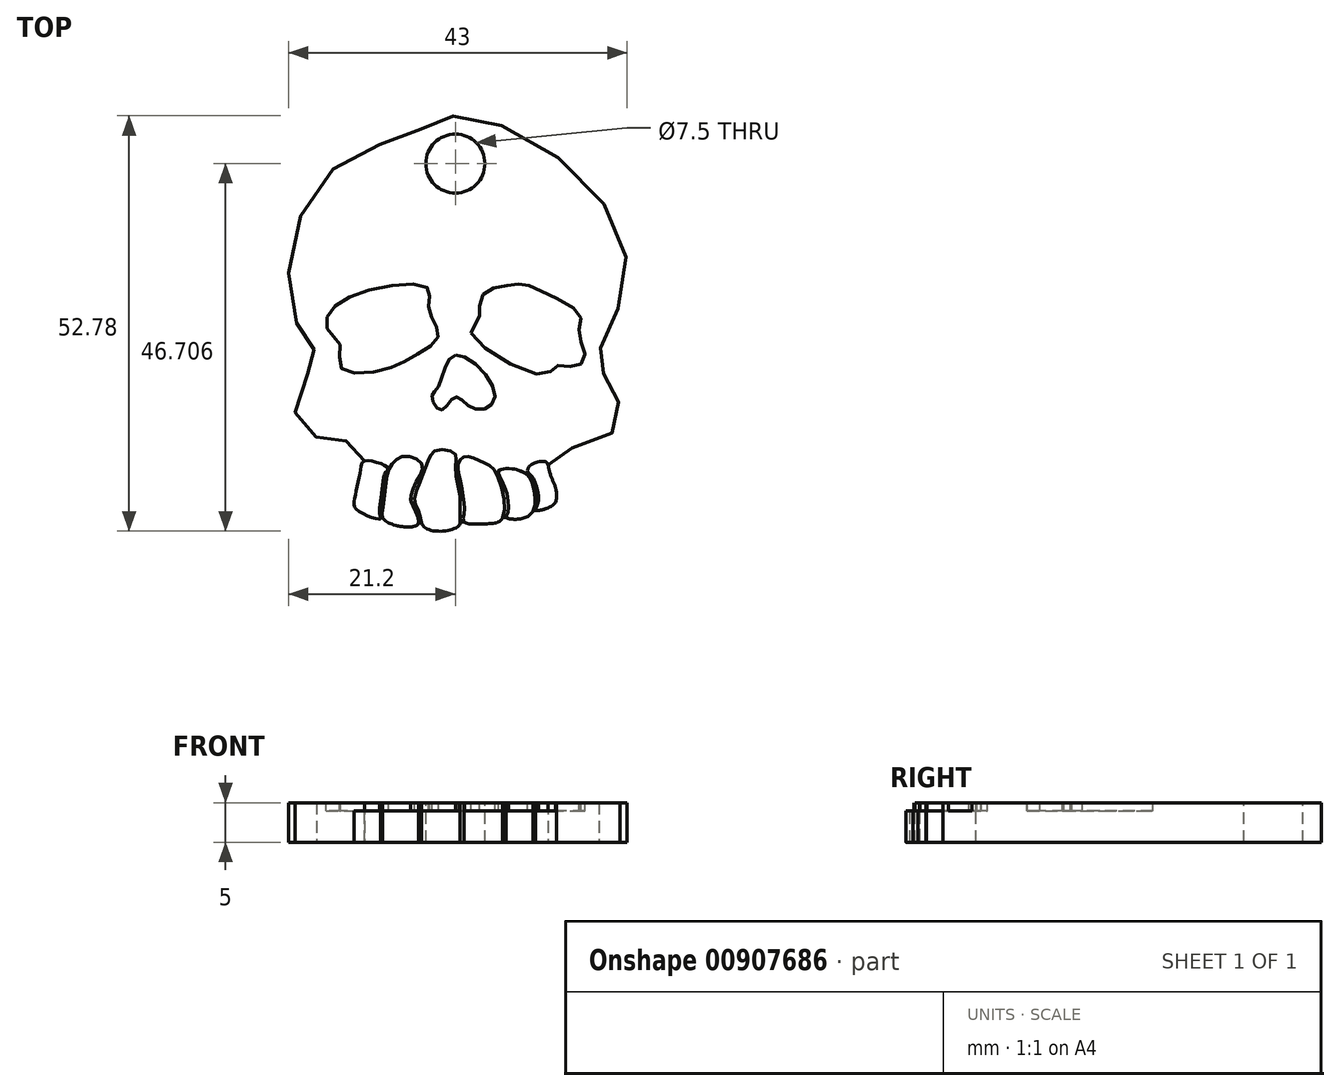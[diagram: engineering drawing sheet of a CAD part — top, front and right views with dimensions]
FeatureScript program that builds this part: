
annotation { "Feature Type Name" : "Feature", "Feature Type Description" : "" }
export const myFeature = defineFeature(function(context is Context, id is Id, definition is map)
    precondition{}
    {
        {
            var Q0;
            Q0=qCreatedBy(makeId("Top.planeOp"),FACE);
            var sketch = newSketch(context, id + "F0", { "sketchPlane" : qUnion([Q0])});
            skPoint(sketch, "E0.middle", {"position": v(0, 0) * mm});
            skFitSpline(sketch, "E1", {"points": [v(-18.77, -2.84) * mm, v(-21.2, 5.84) * mm, v(-15.52, 19.31) * mm, v(-5.25, 23.95) * mm, v(0, 26.05) * mm, v(13.9, 20.07) * mm, v(21.8, 6.43) * mm, v(18.54, -3.21) * mm, v(18.66, -6.34) * mm, v(20.79, -10.47) * mm, v(19.29, -14.73) * mm, v(12.15, -17.23) * mm, v(12.4, -20.36) * mm, v(12.03, -23.24) * mm, v(-11.76, -23.87) * mm, v(-11.5, -17.73) * mm, v(-13.89, -15.23) * mm, v(-18.04, -14.58) * mm, v(-20.36, -10.37) * mm, v(-17.64, -4.46) * mm, v(-18.77, -2.84) * mm]});
            skSolve(sketch);
        }
        {
            var Q0;
            Q0 = qSketchRegion(id + "F0", true);
            extrude(context, id + "F1", {"entities" : qUnion([Q0]), "depth" : 5 * mm, "offsetDistance" : 25 * mm});
        }
        {
            var Q0;
            Q0=makeQuery(id+"F1.opExtrude","CAP_FACE",FACE,{"disambiguationData":[OSD([sQuery(id+"F0.wireOp",EDGE,"E1")])],"isStart":false});
            var sketch = newSketch(context, id + "F2", { "sketchPlane" : qUnion([Q0])});
            skFitSpline(sketch, "E2", {"points": [v(0, -4.32) * mm, v(-2.08, -8.19) * mm, v(-2.98, -9.68) * mm, v(-1.79, -11.31) * mm, v(0, -9.68) * mm, v(2.38, -11.16) * mm, v(5.06, -9.53) * mm, v(0, -4.32) * mm]});
            skFitSpline(sketch, "E3", {"points": [v(2, -1.54) * mm, v(2.9, 0) * mm, v(3.05, 1.3) * mm, v(3.72, 3.6) * mm, v(6.62, 4.5) * mm, v(8.78, 4.64) * mm, v(11.6, 3.45) * mm, v(15.85, 0.7) * mm, v(15.7, -1.61) * mm, v(16.45, -4.29) * mm, v(15.33, -5.78) * mm, v(12.87, -5.7) * mm, v(11.24, -6.82) * mm, v(2, -1.54) * mm]});
            skFitSpline(sketch, "E4", {"points": [v(-2.2, -2.04) * mm, v(-5.03, -4.35) * mm, v(-9.34, -6.29) * mm, v(-14.55, -5.91) * mm, v(-14.63, -3.01) * mm, v(-16.12, -1.37) * mm, v(-15.97, 1.08) * mm, v(-10.31, 4.06) * mm, v(-3.46, 4.13) * mm, v(-3.39, 2.27) * mm, v(-2.8, 0) * mm, v(-2.2, -2.04) * mm]});
            skFitSpline(sketch, "E5", {"points": [v(-3.46, -17.74) * mm, v(-2.44, -16.46) * mm, v(0, -16.9) * mm, v(0, -18.45) * mm, v(0.6, -22.61) * mm, v(0.57, -24.56) * mm, v(0.34, -26.1) * mm, v(-3.77, -26.33) * mm, v(-4.61, -24.3) * mm, v(-5.19, -22.88) * mm, v(-4.26, -19.87) * mm, v(-3.46, -17.74) * mm]});
            skFitSpline(sketch, "E6", {"points": [v(0.46, -17.94) * mm, v(0.46, -19.41) * mm, v(1.03, -22.52) * mm, v(1.09, -24.56) * mm, v(1.12, -25.56) * mm, v(3.67, -25.78) * mm, v(6.01, -25.01) * mm, v(5.03, -19.1) * mm, v(3.3, -17.88) * mm, v(1.4, -17.2) * mm, v(0.46, -17.94) * mm]});
            skFitSpline(sketch, "E7", {"points": [v(5.48, -19.1) * mm, v(6.27, -21.07) * mm, v(6.6, -24.52) * mm, v(6.43, -24.94) * mm, v(7.64, -25.2) * mm, v(9.87, -24.16) * mm, v(9.53, -20.13) * mm, v(8.35, -19.1) * mm, v(6.95, -18.78) * mm, v(5.48, -19.1) * mm]});
            skFitSpline(sketch, "E8", {"points": [v(9.17, -19.1) * mm, v(9.61, -18.26) * mm, v(11.27, -17.84) * mm, v(11.8, -18.32) * mm, v(12.75, -21.3) * mm, v(12.84, -22) * mm, v(12.5, -23.29) * mm, v(10.21, -24.05) * mm, v(10.46, -23.26) * mm, v(9.9, -20.05) * mm, v(9.17, -19.1) * mm]});
            skFitSpline(sketch, "E9", {"points": [v(-4.2, -18.26) * mm, v(-4.9, -20.32) * mm, v(-5.68, -22.58) * mm, v(-5.18, -23.92) * mm, v(-4.68, -25.64) * mm, v(-5.5, -26.16) * mm, v(-7.94, -25.87) * mm, v(-9.22, -25.04) * mm, v(-9.18, -23.53) * mm, v(-8.76, -20.1) * mm, v(-8.05, -18.18) * mm, v(-6.34, -17.16) * mm, v(-4.2, -18.26) * mm]});
            skFitSpline(sketch, "E10", {"points": [v(-8.6, -18.63) * mm, v(-11.5, -17.8) * mm, v(-12.05, -18.87) * mm, v(-12.79, -22.55) * mm, v(-12.47, -24.03) * mm, v(-9.55, -25.16) * mm, v(-9.63, -24.55) * mm, v(-9.42, -22.47) * mm, v(-8.94, -19.42) * mm, v(-8.6, -18.63) * mm]});
            skSolve(sketch);
        }
        {
            var Q0;
            {var subQ0=sQuery(id+"F2.wireOp",EDGE,"E5");var subQ1=makeQuery(id+"F1.opExtrude","CAP_EDGE",EDGE,{"disambiguationData":[OSD([sQuery(id+"F0.wireOp",EDGE,"E1")])],"isStart":false});var subQ2=makeQuery(id+"F2.imprint","INTERSECT",VERTEX,{"disambiguationData":[OD(0.0)],"derivedFrom":[subQ1,subQ0]});Q0=makeQuery(id+"F2.imprint","IMPRINT",FACE,{"disambiguationData":[TD([[makeQuery(id+"F2.imprint","IMPRINT",EDGE,{"disambiguationData":[TD([[subQ2,-1.0]])],"derivedFrom":subQ0}),-1.0]])]});}
            var Q1;
            {var subQ0=sQuery(id+"F2.wireOp",EDGE,"E6");var subQ1=makeQuery(id+"F1.opExtrude","CAP_EDGE",EDGE,{"disambiguationData":[OSD([sQuery(id+"F0.wireOp",EDGE,"E1")])],"isStart":false});var subQ2=makeQuery(id+"F2.imprint","INTERSECT",VERTEX,{"disambiguationData":[OD(0.0)],"derivedFrom":[subQ1,subQ0]});Q1=makeQuery(id+"F2.imprint","IMPRINT",FACE,{"disambiguationData":[TD([[makeQuery(id+"F2.imprint","IMPRINT",EDGE,{"disambiguationData":[TD([[subQ2,1.0]])],"derivedFrom":subQ0}),1.0]])]});}
            var Q2;
            {var subQ0=sQuery(id+"F2.wireOp",EDGE,"E7");var subQ1=makeQuery(id+"F1.opExtrude","CAP_EDGE",EDGE,{"disambiguationData":[OSD([sQuery(id+"F0.wireOp",EDGE,"E1")])],"isStart":false});var subQ2=makeQuery(id+"F2.imprint","INTERSECT",VERTEX,{"disambiguationData":[OD(0.0)],"derivedFrom":[subQ1,subQ0]});Q2=makeQuery(id+"F2.imprint","IMPRINT",FACE,{"disambiguationData":[TD([[makeQuery(id+"F2.imprint","IMPRINT",EDGE,{"disambiguationData":[TD([[subQ2,1.0]])],"derivedFrom":subQ0}),1.0]])]});}
            var Q3;
            {var subQ0=sQuery(id+"F2.wireOp",EDGE,"E8");var subQ1=makeQuery(id+"F1.opExtrude","CAP_EDGE",EDGE,{"disambiguationData":[OSD([sQuery(id+"F0.wireOp",EDGE,"E1")])],"isStart":false});var subQ2=makeQuery(id+"F2.imprint","INTERSECT",VERTEX,{"disambiguationData":[OD(2.0)],"derivedFrom":[subQ1,subQ0]});Q3=makeQuery(id+"F2.imprint","IMPRINT",FACE,{"disambiguationData":[TD([[makeQuery(id+"F2.imprint","IMPRINT",EDGE,{"disambiguationData":[TD([[subQ2,-1.0]])],"derivedFrom":subQ0}),-1.0]])]});}
            var Q4;
            {var subQ0=sQuery(id+"F2.wireOp",EDGE,"E9");var subQ1=makeQuery(id+"F1.opExtrude","CAP_EDGE",EDGE,{"disambiguationData":[OSD([sQuery(id+"F0.wireOp",EDGE,"E1")])],"isStart":false});var subQ2=makeQuery(id+"F2.imprint","INTERSECT",VERTEX,{"disambiguationData":[OD(0.0)],"derivedFrom":[subQ1,subQ0]});Q4=makeQuery(id+"F2.imprint","IMPRINT",FACE,{"disambiguationData":[TD([[makeQuery(id+"F2.imprint","IMPRINT",EDGE,{"disambiguationData":[TD([[subQ2,1.0]])],"derivedFrom":subQ0}),-1.0]])]});}
            var Q5;
            {var subQ0=sQuery(id+"F2.wireOp",EDGE,"E10");var subQ1=makeQuery(id+"F1.opExtrude","CAP_EDGE",EDGE,{"disambiguationData":[OSD([sQuery(id+"F0.wireOp",EDGE,"E1")])],"isStart":false});var subQ2=makeQuery(id+"F2.imprint","INTERSECT",VERTEX,{"disambiguationData":[OD(0.0)],"derivedFrom":[subQ1,subQ0]});Q5=makeQuery(id+"F2.imprint","IMPRINT",FACE,{"disambiguationData":[TD([[makeQuery(id+"F2.imprint","IMPRINT",EDGE,{"disambiguationData":[TD([[subQ2,-1.0]])],"derivedFrom":subQ0}),1.0]])]});}
            extrude(context, id + "F3", {"entities" : qUnion([Q0, Q1, Q2, Q3, Q4, Q5]), "operationType" : NewBodyOperationType.ADD, "oppositeDirection" : true, "depth" : 5 * mm, "offsetDistance" : 25 * mm});
        }
        {
            var Q0;
            Q0 = qSketchRegion(id + "F2", true);
            extrude(context, id + "F4", {"entities" : qUnion([Q0]), "operationType" : NewBodyOperationType.REMOVE, "oppositeDirection" : true, "depth" : 1 * mm, "offsetDistance" : 25 * mm});
        }
        {
            var Q0;
            {var subQ0=sQuery(id+"F0.wireOp",EDGE,"E1");var subQ1=sQuery(id+"F2.wireOp",EDGE,"E10");var subQ2=sQuery(id+"F2.wireOp",EDGE,"E5");var subQ3=sQuery(id+"F2.wireOp",EDGE,"E6");var subQ4=sQuery(id+"F2.wireOp",EDGE,"E7");var subQ5=sQuery(id+"F2.wireOp",EDGE,"E8");var subQ6=sQuery(id+"F2.wireOp",EDGE,"E9");Q0=makeQuery(id+"F4.boolean.opBoolean","SPLIT",FACE,{"disambiguationData":[TD([makeQuery(id+"F1.opExtrude","SWEPT_FACE",FACE,{"disambiguationData":[OSD([subQ0])]}),makeQuery(id+"F4.opExtrude","SWEPT_FACE",FACE,{"disambiguationData":[OSD([sQuery(id+"F2.wireOp",EDGE,"E2")])]}),makeQuery(id+"F4.opExtrude","SWEPT_FACE",FACE,{"disambiguationData":[OSD([sQuery(id+"F2.wireOp",EDGE,"E3")])]}),makeQuery(id+"F4.opExtrude","SWEPT_FACE",FACE,{"disambiguationData":[OSD([sQuery(id+"F2.wireOp",EDGE,"E4")])]}),makeQuery(id+"F4.opExtrude","SWEPT_FACE",FACE,{"disambiguationData":[OSD([subQ2])]}),makeQuery(id+"F4.opExtrude","SWEPT_FACE",FACE,{"disambiguationData":[OSD([subQ3])]}),makeQuery(id+"F4.opExtrude","SWEPT_FACE",FACE,{"disambiguationData":[OSD([subQ4])]}),makeQuery(id+"F4.opExtrude","SWEPT_FACE",FACE,{"disambiguationData":[OSD([subQ5])]}),makeQuery(id+"F4.opExtrude","SWEPT_FACE",FACE,{"disambiguationData":[OSD([subQ6])]}),makeQuery(id+"F4.opExtrude","SWEPT_FACE",FACE,{"disambiguationData":[OSD([subQ1])]})])],"derivedFrom":makeQuery(id+"F3.boolean.opBoolean","MERGE",FACE,{"derivedFrom":[makeQuery(id+"F1.opExtrude","CAP_FACE",FACE,{"disambiguationData":[OSD([subQ0])],"isStart":false}),makeQuery(id+"F3.opExtrude","CAP_FACE",FACE,{"disambiguationData":[OSD([subQ0,subQ2])],"isStart":true}),makeQuery(id+"F3.opExtrude","CAP_FACE",FACE,{"disambiguationData":[OSD([subQ0,subQ3])],"isStart":true}),makeQuery(id+"F3.opExtrude","CAP_FACE",FACE,{"disambiguationData":[OSD([subQ0,subQ4])],"isStart":true}),makeQuery(id+"F3.opExtrude","CAP_FACE",FACE,{"disambiguationData":[OSD([subQ0,subQ5])],"isStart":true}),makeQuery(id+"F3.opExtrude","CAP_FACE",FACE,{"disambiguationData":[OSD([subQ0,subQ6])],"isStart":true}),makeQuery(id+"F3.opExtrude","CAP_FACE",FACE,{"disambiguationData":[OSD([subQ0,subQ1])],"isStart":true})]})});}
            var sketch = newSketch(context, id + "F5", { "sketchPlane" : qUnion([Q0])});
            skCircle(sketch, "E11", {"center": v(0, 19.99) * mm, "radius": 3.75 * mm});
            skSolve(sketch);
        }
        {
            var Q0;
            Q0 = qSketchRegion(id + "F5", true);
            extrude(context, id + "F6", {"entities" : qUnion([Q0]), "operationType" : NewBodyOperationType.REMOVE, "oppositeDirection" : true, "depth" : 25 * mm, "offsetDistance" : 25 * mm});
        }
    });
